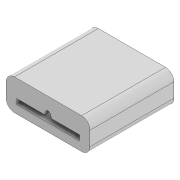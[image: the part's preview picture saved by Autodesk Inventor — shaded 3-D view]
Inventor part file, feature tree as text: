
AUTODESK INVENTOR PART (.ipt)
format: ipt  version: 2022 (Build 260153000, 153)  size: 109,568 bytes
history: native  units: mm
features: extrude x1, fillet x1, sketch x1
ambient origin geometry x8: Origin, YZ Plane, XZ Plane, XY Plane, X Axis, Y Axis, Z Axis, Center Point
bodies: Solid1 (feature_tree)
feature tree (3):
  extrude  "Extrusion1"  Depth=7.5mm
  fillet  "Fillet1"  Radius=3.75mm
  sketch  "Sketch1"  dims[d0=10.0mm d1=7.5mm d2=3.75mm d3=5.0mm d4=1.0mm d5=0.6mm d6=0.6mm d7=1.5mm d8=12.217305mm d9=12.217305mm d10=10.0mm d11=0.0mm d12=1.0mm]
